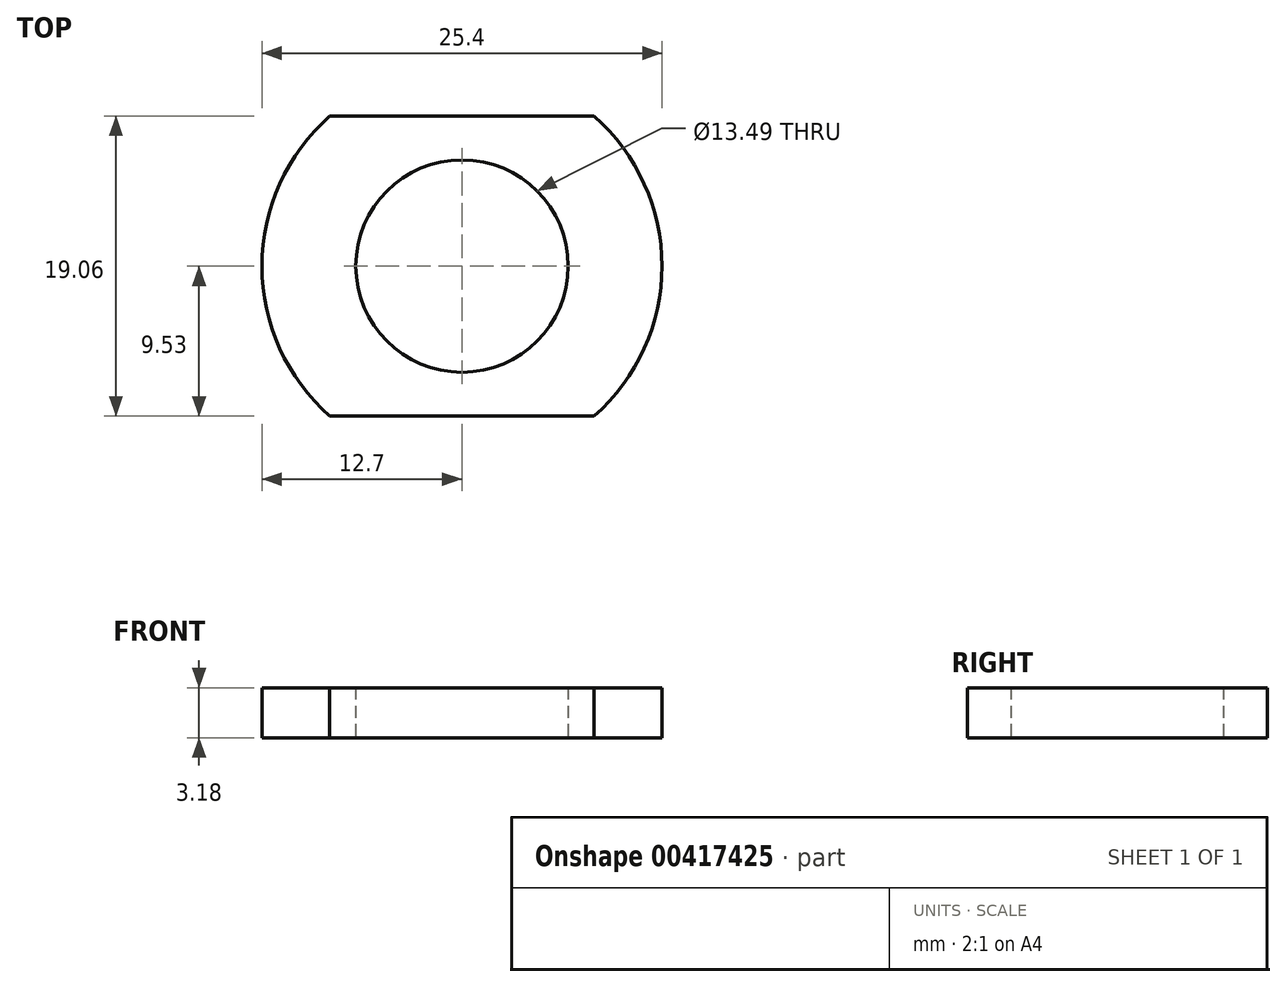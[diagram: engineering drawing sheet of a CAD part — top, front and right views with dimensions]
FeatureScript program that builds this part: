
annotation { "Feature Type Name" : "Feature", "Feature Type Description" : "" }
export const myFeature = defineFeature(function(context is Context, id is Id, definition is map)
    precondition{}
    {
        {
            var Q0;
            Q0=qCreatedBy(makeId("Top.planeOp"),FACE);
            var sketch = newSketch(context, id + "F0", { "sketchPlane" : qUnion([Q0])});
            skCircle(sketch, "E0", {"center": v(0, 0) * mm, "radius": 6.74 * mm});
            skArc(sketch, "E1", {"start": v(-8.4, 9.52) * mm, "mid": v(-12.7, 0) * mm, "end": v(-8.4, -9.53) * mm});
            skLineSegment(sketch, "E2", {"start": v(-8.4, 9.53) * mm, "end": v(8.4, 9.53) * mm});
            skLineSegment(sketch, "E3", {"start": v(-8.4, -9.53) * mm, "end": v(8.4, -9.53) * mm});
            skArc(sketch, "E4.trimOffspring", {"start": v(8.4, -9.53) * mm, "mid": v(12.7, 0) * mm, "end": v(8.4, 9.53) * mm});
            skSolve(sketch);
        }
        {
            var Q0;
            Q0=makeQuery(id+"F0.imprint","IMPRINT",FACE,{"disambiguationData":[TD([[makeQuery(id+"F0.imprint","IMPRINT",EDGE,{"derivedFrom":sQuery(id+"F0.wireOp",EDGE,"E0")}),-1.0]])]});
            extrude(context, id + "F1", {"entities" : qUnion([Q0]), "depth" : 3.17 * mm, "offsetDistance" : 25.4 * mm});
        }
    });
